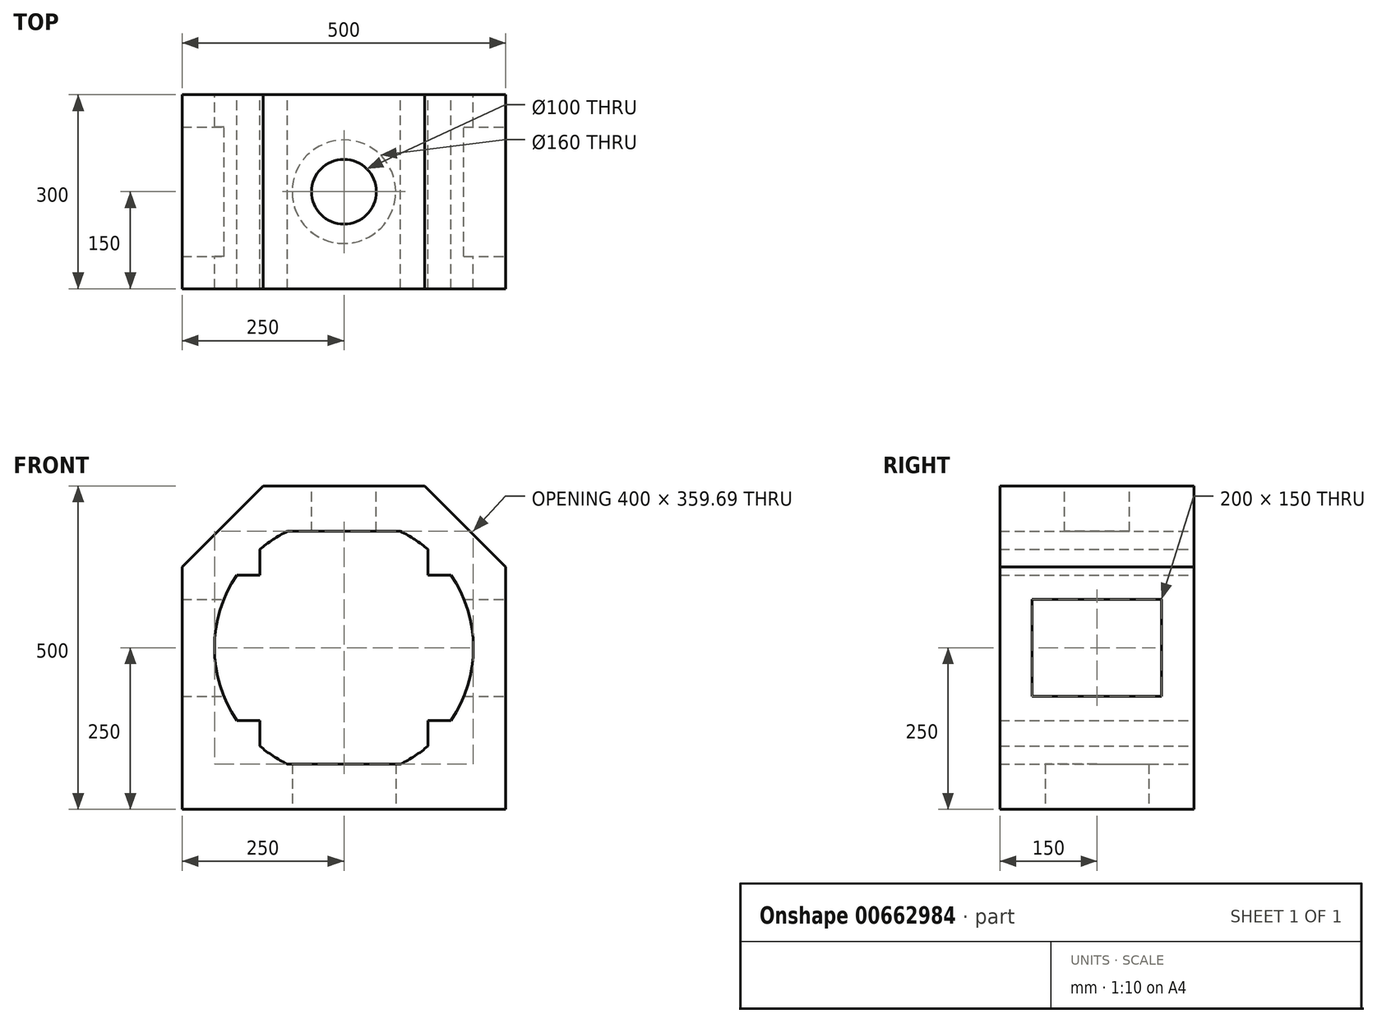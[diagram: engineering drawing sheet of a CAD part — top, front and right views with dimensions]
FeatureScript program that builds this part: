
annotation { "Feature Type Name" : "Feature", "Feature Type Description" : "" }
export const myFeature = defineFeature(function(context is Context, id is Id, definition is map)
    precondition{}
    {
        {
            var Q0;
            Q0=qCreatedBy(makeId("Front.planeOp"),FACE);
            var sketch = newSketch(context, id + "F0", { "sketchPlane" : qUnion([Q0])});
            skLineSegment(sketch, "E0.bottom", {"start": v(250, -250) * mm, "end": v(-250, -250) * mm});
            skLineSegment(sketch, "E0.left", {"start": v(250, -250) * mm, "end": v(250, 250) * mm});
            skLineSegment(sketch, "E0.right", {"start": v(-250, -250) * mm, "end": v(-250, 250) * mm});
            skPoint(sketch, "E0.middle", {"position": v(0, 0) * mm});
            skLineSegment(sketch, "E1", {"start": v(250, 250) * mm, "end": v(-250, 250) * mm});
            skCircle(sketch, "E2", {"center": v(0, 0) * mm, "radius": 200 * mm});
            skLineSegment(sketch, "E3", {"start": v(-165.36, 112.5) * mm, "end": v(-130, 112.5) * mm});
            skLineSegment(sketch, "E4", {"start": v(-130, 112.5) * mm, "end": v(-130, 151.99) * mm});
            skLineSegment(sketch, "E5", {"start": v(-165.36, -112.5) * mm, "end": v(-130, -112.5) * mm});
            skLineSegment(sketch, "E6", {"start": v(-130, -112.5) * mm, "end": v(-130, -151.99) * mm});
            skLineSegment(sketch, "E7", {"start": v(165.36, 112.5) * mm, "end": v(130, 112.5) * mm});
            skLineSegment(sketch, "E8", {"start": v(130, 112.5) * mm, "end": v(130, 151.99) * mm});
            skLineSegment(sketch, "E9", {"start": v(165.36, -112.5) * mm, "end": v(130, -112.5) * mm});
            skLineSegment(sketch, "E10", {"start": v(130, -112.5) * mm, "end": v(130, -151.99) * mm});
            skLineSegment(sketch, "E11", {"start": v(-87.5, -179.84) * mm, "end": v(87.5, -179.84) * mm});
            skLineSegment(sketch, "E12", {"start": v(-87.5, 179.84) * mm, "end": v(87.5, 179.84) * mm});
            skLineSegment(sketch, "E13", {"start": v(-250, 125) * mm, "end": v(-125, 250) * mm});
            skLineSegment(sketch, "E14", {"start": v(250, 125) * mm, "end": v(125, 250) * mm});
            skSolve(sketch);
        }
        {
            var Q0;
            {var subQ11=sQuery(id+"F0.wireOp",EDGE,"E0.bottom");Q0=makeQuery(id+"F0.imprint","IMPRINT",FACE,{"disambiguationData":[TD([[makeQuery(id+"F0.imprint","IMPRINT",EDGE,{"derivedFrom":subQ11}),-1.0]])]});}
            var Q1;
            {var subQ0=sQuery(id+"F0.wireOp",EDGE,"E3");Q1=makeQuery(id+"F0.imprint","IMPRINT",FACE,{"disambiguationData":[TD([[makeQuery(id+"F0.imprint","IMPRINT",EDGE,{"derivedFrom":subQ0}),1.0]])]});}
            var Q2;
            {var subQ0=sQuery(id+"F0.wireOp",EDGE,"E12");Q2=makeQuery(id+"F0.imprint","IMPRINT",FACE,{"disambiguationData":[TD([[makeQuery(id+"F0.imprint","IMPRINT",EDGE,{"derivedFrom":subQ0}),1.0]])]});}
            var Q3;
            {var subQ0=sQuery(id+"F0.wireOp",EDGE,"E7");Q3=makeQuery(id+"F0.imprint","IMPRINT",FACE,{"disambiguationData":[TD([[makeQuery(id+"F0.imprint","IMPRINT",EDGE,{"derivedFrom":subQ0}),-1.0]])]});}
            var Q4;
            {var subQ0=sQuery(id+"F0.wireOp",EDGE,"E9");Q4=makeQuery(id+"F0.imprint","IMPRINT",FACE,{"disambiguationData":[TD([[makeQuery(id+"F0.imprint","IMPRINT",EDGE,{"derivedFrom":subQ0}),1.0]])]});}
            var Q5;
            {var subQ0=sQuery(id+"F0.wireOp",EDGE,"E11");Q5=makeQuery(id+"F0.imprint","IMPRINT",FACE,{"disambiguationData":[TD([[makeQuery(id+"F0.imprint","IMPRINT",EDGE,{"derivedFrom":subQ0}),-1.0]])]});}
            var Q6;
            {var subQ0=sQuery(id+"F0.wireOp",EDGE,"E5");Q6=makeQuery(id+"F0.imprint","IMPRINT",FACE,{"disambiguationData":[TD([[makeQuery(id+"F0.imprint","IMPRINT",EDGE,{"derivedFrom":subQ0}),-1.0]])]});}
            extrude(context, id + "F1", {"entities" : qUnion([Q0, Q1, Q2, Q3, Q4, Q5, Q6]), "depth" : 300 * mm, "offsetDistance" : 25 * mm});
        }
        {
            var Q0;
            Q0=makeQuery(id+"F1.opExtrude","SWEPT_FACE",FACE,{"disambiguationData":[OSD([sQuery(id+"F0.wireOp",EDGE,"E1")])]});
            var sketch = newSketch(context, id + "F2", { "sketchPlane" : qUnion([Q0])});
            skCircle(sketch, "E15", {"center": v(0, -150) * mm, "radius": 50 * mm});
            skPoint(sketch, "E15.centerSnap0", {"position": v(-125, -150) * mm});
            skPoint(sketch, "E15.centerSnap1", {"position": v(0, -300) * mm});
            skSolve(sketch);
        }
        {
            var Q0;
            Q0=makeQuery(id+"F2.imprint","IMPRINT",FACE,{"disambiguationData":[TD([[makeQuery(id+"F2.imprint","IMPRINT",EDGE,{"derivedFrom":sQuery(id+"F2.wireOp",EDGE,"E15")}),1.0]])]});
            var Q1;
            Q1=makeQuery(id+"F1.opExtrude","SWEPT_FACE",FACE,{"disambiguationData":[OSD([sQuery(id+"F0.wireOp",EDGE,"E12")])]});
            extrude(context, id + "F3", {"entities" : qUnion([Q0]), "operationType" : NewBodyOperationType.REMOVE, "endBound" : BoundingType.UP_TO_SURFACE, "oppositeDirection" : true, "depth" : 25 * mm, "endBoundEntityFace" : qUnion([Q1]), "offsetDistance" : 25 * mm});
        }
        {
            var Q0;
            Q0=makeQuery(id+"F1.opExtrude","SWEPT_FACE",FACE,{"disambiguationData":[OSD([sQuery(id+"F0.wireOp",EDGE,"E0.bottom")])]});
            var sketch = newSketch(context, id + "F4", { "sketchPlane" : qUnion([Q0])});
            skCircle(sketch, "E16", {"center": v(0, 150) * mm, "radius": 80 * mm});
            skPoint(sketch, "E16.centerSnap0", {"position": v(0, 300) * mm});
            skPoint(sketch, "E16.centerSnap1", {"position": v(-250, 150) * mm});
            skSolve(sketch);
        }
        {
            var Q0;
            Q0=makeQuery(id+"F4.imprint","IMPRINT",FACE,{"disambiguationData":[TD([[makeQuery(id+"F4.imprint","IMPRINT",EDGE,{"derivedFrom":sQuery(id+"F4.wireOp",EDGE,"E16")}),1.0]])]});
            var Q1;
            Q1=makeQuery(id+"F1.opExtrude","SWEPT_FACE",FACE,{"disambiguationData":[OSD([sQuery(id+"F0.wireOp",EDGE,"E11")])]});
            extrude(context, id + "F5", {"entities" : qUnion([Q0]), "operationType" : NewBodyOperationType.REMOVE, "endBound" : BoundingType.UP_TO_SURFACE, "oppositeDirection" : true, "depth" : 25 * mm, "endBoundEntityFace" : qUnion([Q1]), "offsetDistance" : 25 * mm});
        }
        {
            var Q0;
            Q0=makeQuery(id+"F1.opExtrude","SWEPT_FACE",FACE,{"disambiguationData":[OSD([sQuery(id+"F0.wireOp",EDGE,"E0.left")])]});
            var sketch = newSketch(context, id + "F6", { "sketchPlane" : qUnion([Q0])});
            skLineSegment(sketch, "E17.bottom", {"start": v(-50, -75) * mm, "end": v(-250, -75) * mm});
            skLineSegment(sketch, "E17.top", {"start": v(-50, 75) * mm, "end": v(-250, 75) * mm});
            skLineSegment(sketch, "E17.left", {"start": v(-50, -75) * mm, "end": v(-50, 75) * mm});
            skLineSegment(sketch, "E17.right", {"start": v(-250, -75) * mm, "end": v(-250, 75) * mm});
            skPoint(sketch, "E17.middle", {"position": v(-150, 0) * mm});
            skPoint(sketch, "E17.middle.positionSnap0", {"position": v(-150, 125) * mm});
            skPoint(sketch, "E17.centerSnap0", {"position": v(-150, 125) * mm});
            skSolve(sketch);
        }
        {
            var Q0;
            Q0=makeQuery(id+"F6.imprint","IMPRINT",FACE,{"disambiguationData":[TD([[makeQuery(id+"F6.imprint","IMPRINT",EDGE,{"derivedFrom":sQuery(id+"F6.wireOp",EDGE,"E17.bottom")}),-1.0]])]});
            extrude(context, id + "F7", {"entities" : qUnion([Q0]), "operationType" : NewBodyOperationType.REMOVE, "endBound" : BoundingType.THROUGH_ALL, "oppositeDirection" : true, "depth" : 25 * mm, "offsetDistance" : 25 * mm});
        }
    });
